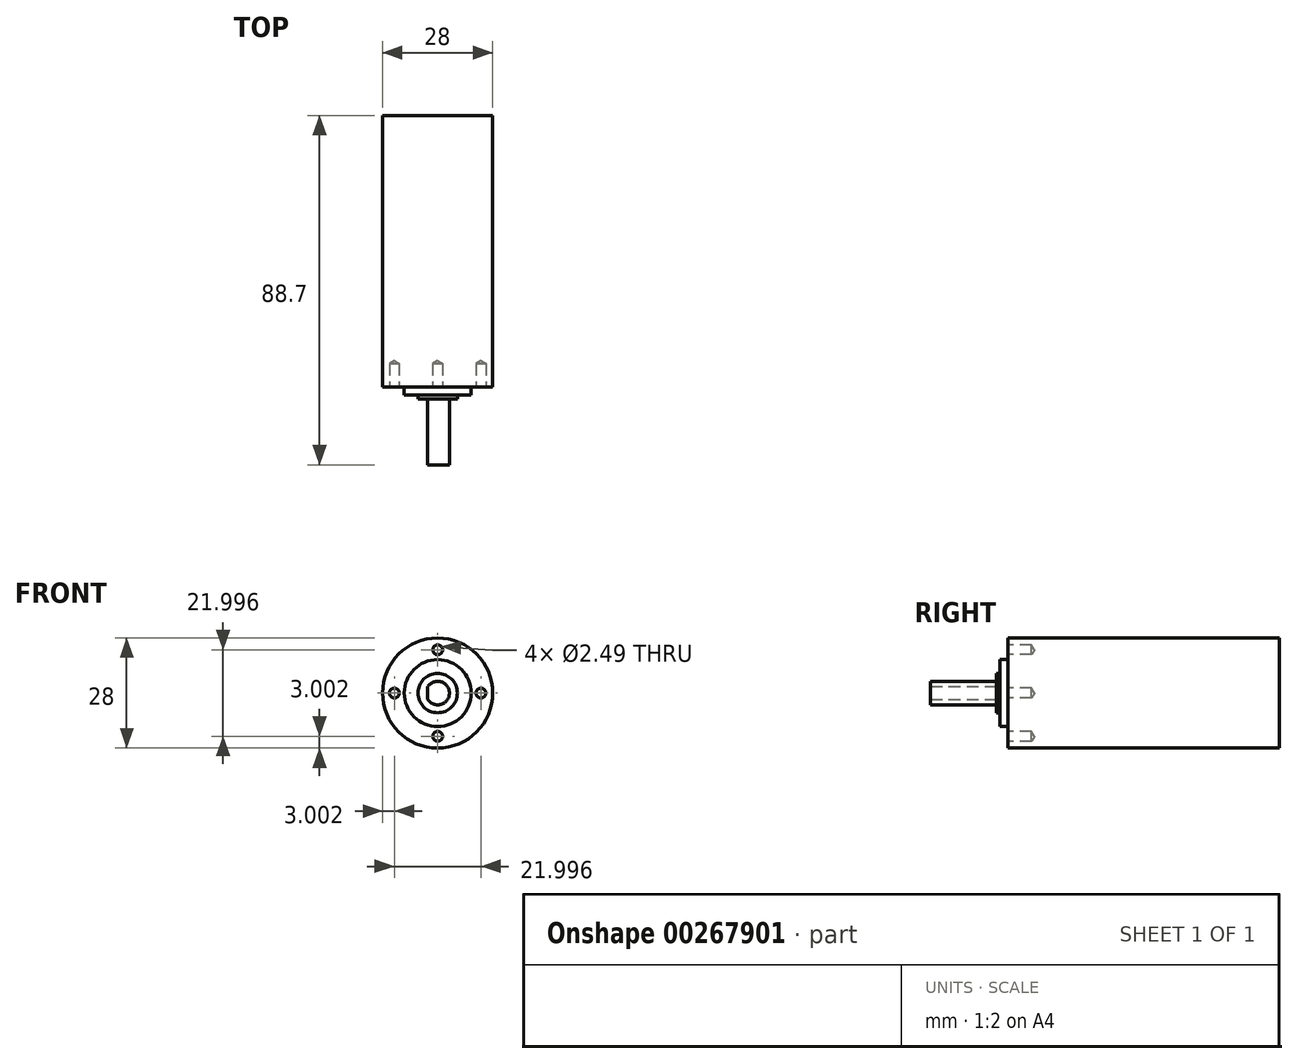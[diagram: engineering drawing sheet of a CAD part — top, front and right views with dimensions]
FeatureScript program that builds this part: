
annotation { "Feature Type Name" : "Feature", "Feature Type Description" : "" }
export const myFeature = defineFeature(function(context is Context, id is Id, definition is map)
    precondition{}
    {
        {
            var Q0;
            Q0=qCreatedBy(makeId("Front.planeOp"),FACE);
            var sketch = newSketch(context, id + "F0", { "sketchPlane" : qUnion([Q0])});
            skCircle(sketch, "E0", {"center": v(0, 0) * mm, "radius": 14 * mm});
            skSolve(sketch);
        }
        {
            var Q0;
            Q0=makeQuery(id+"F0.imprint","IMPRINT",FACE,{"disambiguationData":[TD([[makeQuery(id+"F0.imprint","IMPRINT",EDGE,{"derivedFrom":sQuery(id+"F0.wireOp",EDGE,"E0")}),1.0]])]});
            extrude(context, id + "F1", {"entities" : qUnion([Q0]), "depth" : 31.5 * mm});
        }
        {
            var Q0;
            Q0=makeQuery(id+"F1.opExtrude","CAP_FACE",FACE,{"disambiguationData":[OSD([sQuery(id+"F0.wireOp",EDGE,"E0")])],"isStart":true});
            extrude(context, id + "F2", {"entities" : qUnion([Q0]), "operationType" : NewBodyOperationType.ADD, "depth" : 37.5 * mm});
        }
        {
            var Q0;
            Q0=makeQuery(id+"F1.opExtrude","CAP_FACE",FACE,{"disambiguationData":[OSD([sQuery(id+"F0.wireOp",EDGE,"E0")])],"isStart":false});
            var sketch = newSketch(context, id + "F3", { "sketchPlane" : qUnion([Q0])});
            skCircle(sketch, "E1", {"center": v(0, 0) * mm, "radius": 8.5 * mm});
            skCircle(sketch, "E2", {"center": v(0, 0) * mm, "radius": 5 * mm});
            skCircle(sketch, "E3", {"center": v(0, 0) * mm, "radius": 3 * mm});
            skLineSegment(sketch, "E4", {"start": v(-2.51, 1.63) * mm, "end": v(-2.51, -1.63) * mm});
            skCircle(sketch, "E5", {"center": v(0, 11) * mm, "radius": 1.24 * mm});
            skCircle(sketch, "E6", {"center": v(11, 0) * mm, "radius": 1.24 * mm});
            skCircle(sketch, "E7", {"center": v(0, -11) * mm, "radius": 1.24 * mm});
            skCircle(sketch, "E8", {"center": v(-11, 0) * mm, "radius": 1.24 * mm});
            skSolve(sketch);
        }
        {
            var Q0;
            {var subQ0=sQuery(id+"F3.wireOp",EDGE,"E4");Q0=makeQuery(id+"F3.imprint","IMPRINT",FACE,{"disambiguationData":[TD([[makeQuery(id+"F3.imprint","IMPRINT",EDGE,{"derivedFrom":subQ0}),1.0]])]});}
            extrude(context, id + "F4", {"entities" : qUnion([Q0]), "operationType" : NewBodyOperationType.ADD, "depth" : 19.71 * mm});
        }
        {
            var Q0;
            Q0=makeQuery(id+"F3.imprint","IMPRINT",FACE,{"disambiguationData":[TD([[makeQuery(id+"F3.imprint","IMPRINT",EDGE,{"derivedFrom":sQuery(id+"F3.wireOp",EDGE,"E2")}),1.0]])]});
            var Q1;
            {var subQ0=sQuery(id+"F3.wireOp",EDGE,"E4");Q1=makeQuery(id+"F3.imprint","IMPRINT",FACE,{"disambiguationData":[TD([[makeQuery(id+"F3.imprint","IMPRINT",EDGE,{"derivedFrom":subQ0}),-1.0]])]});}
            extrude(context, id + "F5", {"entities" : qUnion([Q0, Q1]), "operationType" : NewBodyOperationType.ADD, "depth" : 3 * mm});
        }
        {
            var Q0;
            Q0=makeQuery(id+"F3.imprint","IMPRINT",FACE,{"disambiguationData":[TD([[makeQuery(id+"F3.imprint","IMPRINT",EDGE,{"derivedFrom":sQuery(id+"F3.wireOp",EDGE,"E1")}),1.0]])]});
            extrude(context, id + "F6", {"entities" : qUnion([Q0]), "operationType" : NewBodyOperationType.ADD, "depth" : 2 * mm});
        }
        {
            var Q0;
            Q0=sQuery(id+"F3.wireOp",VERTEX,"E6.center");
            var Q1;
            Q1=sQuery(id+"F3.wireOp",VERTEX,"E7.center");
            var Q2;
            Q2=sQuery(id+"F3.wireOp",VERTEX,"E5.center");
            var Q3;
            Q3=sQuery(id+"F3.wireOp",VERTEX,"E8.center");
            var Q4;
            Q4=makeQuery(id+"F1.opExtrude","SWEPT_BODY",BODY,{"disambiguationData":[OSD([sQuery(id+"F0.wireOp",EDGE,"E0")])]});
            hole(context, id + "F7", {"style" : HoleStyle.SIMPLE, "endStyle" : HoleEndStyle.BLIND, "holeDiameter" : 2.5 * mm, "holeDepth" : 6 * mm, "tappedDepth" : 12.7 * mm, "tapClearance" : 3, "locations" : qUnion([Q0, Q1, Q2, Q3]), "scope" : qUnion([Q4])});
        }
    });
